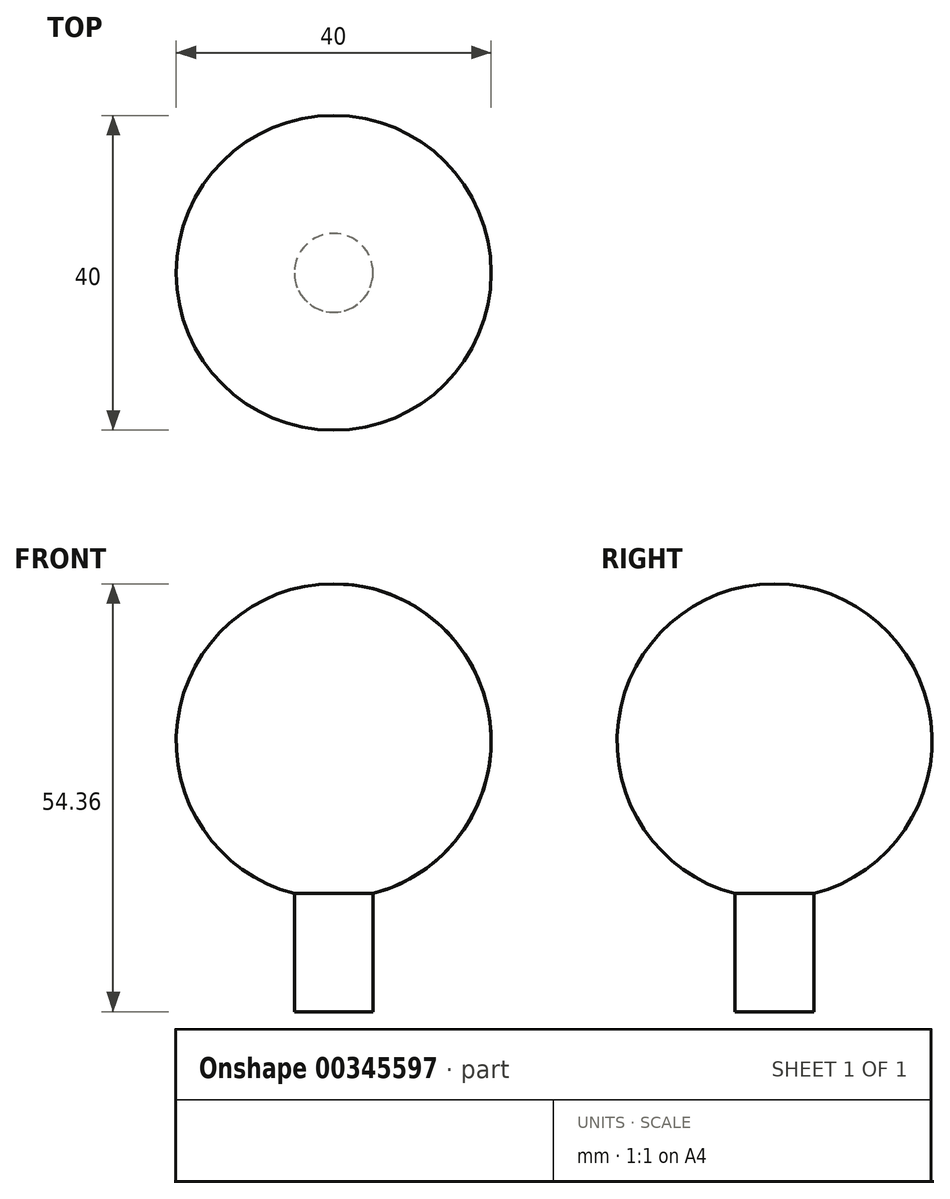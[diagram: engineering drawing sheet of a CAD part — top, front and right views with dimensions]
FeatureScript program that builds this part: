
annotation { "Feature Type Name" : "Feature", "Feature Type Description" : "" }
export const myFeature = defineFeature(function(context is Context, id is Id, definition is map)
    precondition{}
    {
        {
            var Q0;
            Q0=qCreatedBy(makeId("Front.planeOp"),FACE);
            var sketch = newSketch(context, id + "F0", { "sketchPlane" : qUnion([Q0])});
            skArc(sketch, "E0", {"start": v(0, 0) * mm, "mid": v(20, -20) * mm, "end": v(0, -40) * mm});
            skLineSegment(sketch, "E1", {"start": v(0, -40) * mm, "end": v(0, 0) * mm});
            skLineSegment(sketch, "E2", {"start": v(0, -54.36) * mm, "end": v(5, -54.36) * mm});
            skLineSegment(sketch, "E3", {"start": v(5, -39.36) * mm, "end": v(5, -54.36) * mm});
            skLineSegment(sketch, "E4", {"start": v(0, -54.36) * mm, "end": v(0, -40) * mm});
            skSolve(sketch);
        }
        {
            var Q0;
            {var subQ0=sQuery(id+"F0.wireOp",EDGE,"E1");Q0=makeQuery(id+"F0.imprint","IMPRINT",FACE,{"disambiguationData":[TD([[makeQuery(id+"F0.imprint","IMPRINT",EDGE,{"derivedFrom":subQ0}),-1.0]])]});}
            var Q1;
            Q1=makeQuery(id+"F0.imprint","IMPRINT",FACE,{"disambiguationData":[TD([[makeQuery(id+"F0.imprint","IMPRINT",EDGE,{"derivedFrom":sQuery(id+"F0.wireOp",EDGE,"E2")}),1.0]])]});
            var Q2;
            Q2=sQuery(id+"F0.wireOp",EDGE,"E1");
            revolve(context, id + "F1", {"entities" : qUnion([Q0, Q1]), "axis" : qUnion([Q2]), "revolveType" : RevolveType.FULL});
        }
    });
